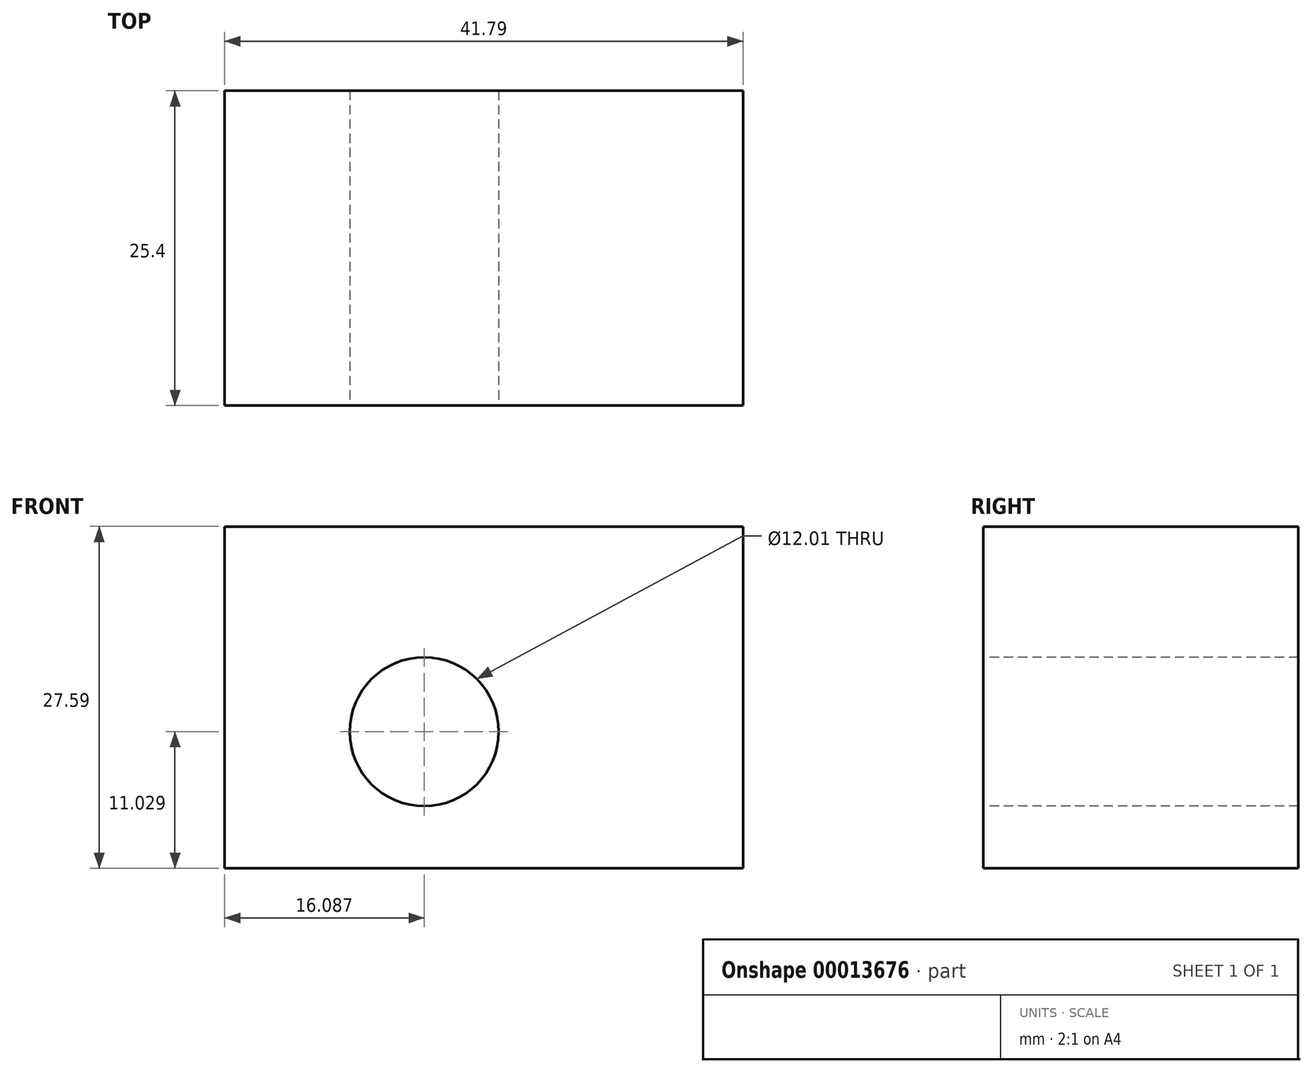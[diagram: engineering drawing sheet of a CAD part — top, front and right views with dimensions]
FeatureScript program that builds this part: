
annotation { "Feature Type Name" : "Feature", "Feature Type Description" : "" }
export const myFeature = defineFeature(function(context is Context, id is Id, definition is map)
    precondition{}
    {
        {
            var Q0;
            Q0=qCreatedBy(makeId("Front.planeOp"),FACE);
            var sketch = newSketch(context, id + "F0", { "sketchPlane" : qUnion([Q0])});
            skLineSegment(sketch, "E0.bottom", {"start": v(0, 0) * mm, "end": v(41.8, 0) * mm});
            skLineSegment(sketch, "E0.top", {"start": v(0, 27.59) * mm, "end": v(41.8, 27.59) * mm});
            skLineSegment(sketch, "E0.left", {"start": v(0, 0) * mm, "end": v(0, 27.59) * mm});
            skLineSegment(sketch, "E0.right", {"start": v(41.8, 0) * mm, "end": v(41.8, 27.59) * mm});
            skSolve(sketch);
        }
        {
            var Q0;
            Q0=makeQuery(id+"F0.imprint","IMPRINT",FACE,{"disambiguationData":[TD([[makeQuery(id+"F0.imprint","IMPRINT",EDGE,{"derivedFrom":sQuery(id+"F0.wireOp",EDGE,"E0.bottom")}),1.0]])]});
            extrude(context, id + "F1", {"entities" : qUnion([Q0]), "depth" : 25.4 * mm});
        }
        {
            var Q0;
            Q0=makeQuery(id+"F1.opExtrude","CAP_FACE",FACE,{"disambiguationData":[OSD([sQuery(id+"F0.wireOp",EDGE,"E0.bottom"),sQuery(id+"F0.wireOp",EDGE,"E0.top"),sQuery(id+"F0.wireOp",EDGE,"E0.left"),sQuery(id+"F0.wireOp",EDGE,"E0.right")])],"isStart":false});
            var sketch = newSketch(context, id + "F2", { "sketchPlane" : qUnion([Q0])});
            skCircle(sketch, "E1", {"center": v(16.09, 11.03) * mm, "radius": 6 * mm});
            skSolve(sketch);
        }
        {
            var Q0;
            Q0=makeQuery(id+"F2.imprint","IMPRINT",FACE,{"disambiguationData":[TD([[makeQuery(id+"F2.imprint","IMPRINT",EDGE,{"derivedFrom":sQuery(id+"F2.wireOp",EDGE,"E1")}),1.0]])]});
            extrude(context, id + "F3", {"entities" : qUnion([Q0]), "operationType" : NewBodyOperationType.REMOVE, "oppositeDirection" : true, "depth" : 49.95 * mm});
        }
    });
